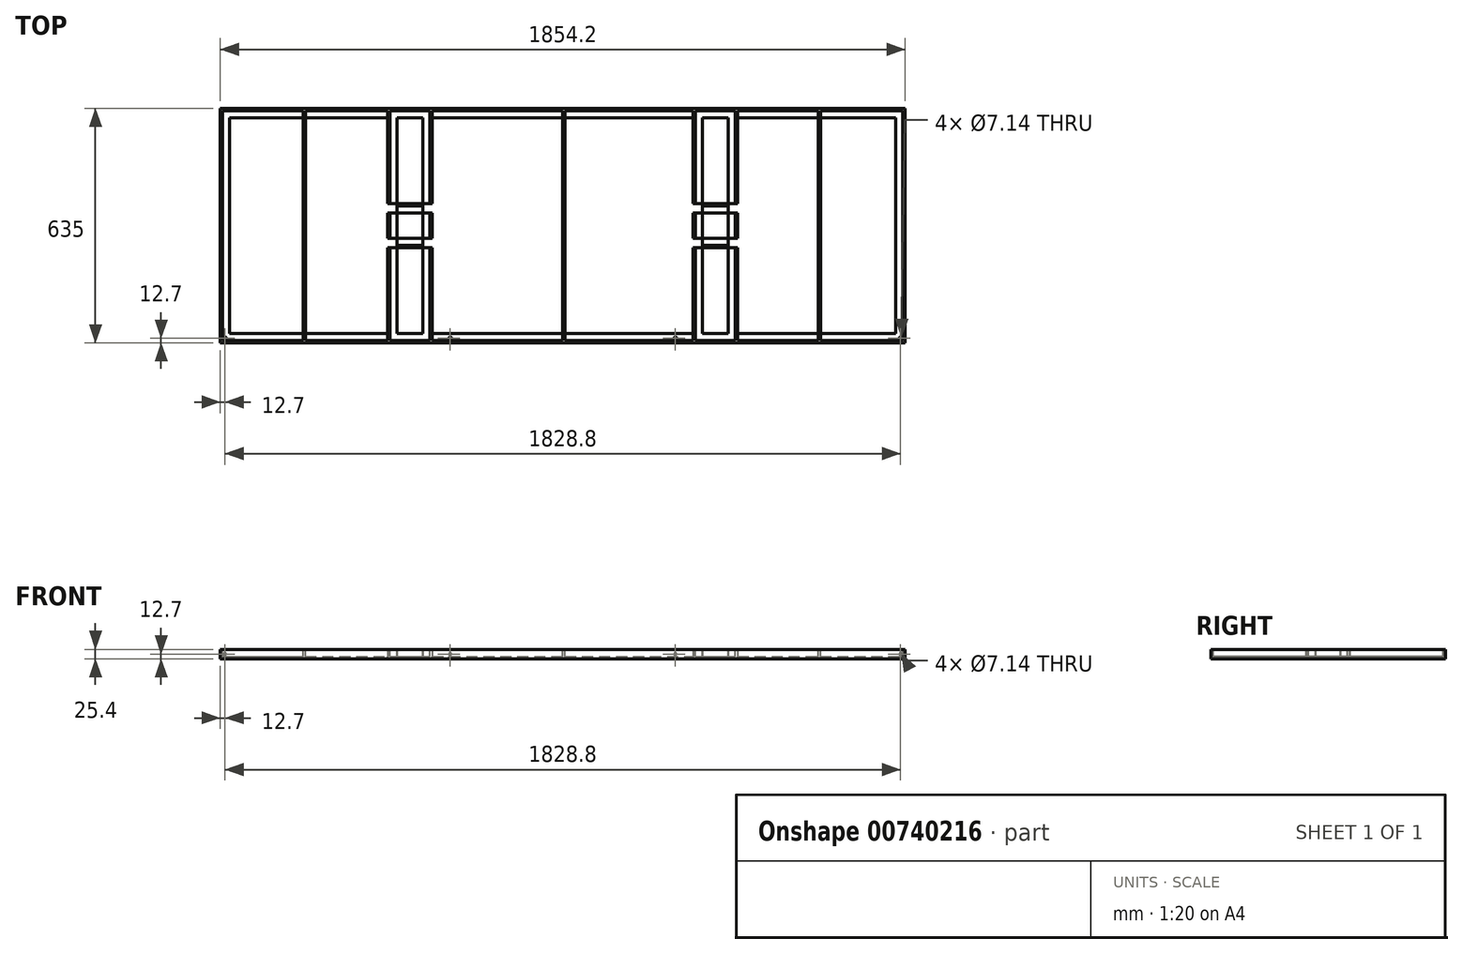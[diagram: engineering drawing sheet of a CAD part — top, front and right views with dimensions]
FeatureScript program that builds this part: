
annotation { "Feature Type Name" : "Feature", "Feature Type Description" : "" }
export const myFeature = defineFeature(function(context is Context, id is Id, definition is map)
    precondition{}
    {
        {
            var Q0;
            Q0=qCreatedBy(makeId("Top.planeOp"),FACE);
            var sketch = newSketch(context, id + "F0", { "sketchPlane" : qUnion([Q0])});
            skLineSegment(sketch, "E0.bottom", {"start": v(0, 0) * mm, "end": v(1854.2, 0) * mm});
            skLineSegment(sketch, "E0.top", {"start": v(0, -25.4) * mm, "end": v(1854.2, -25.4) * mm});
            skLineSegment(sketch, "E0.left", {"start": v(0, 0) * mm, "end": v(0, -25.4) * mm});
            skLineSegment(sketch, "E0.right", {"start": v(1854.2, 0) * mm, "end": v(1854.2, -25.4) * mm});
            skLineSegment(sketch, "E1.bottom", {"start": v(0, 0) * mm, "end": v(25.4, 0) * mm});
            skLineSegment(sketch, "E1.top", {"start": v(0, -635) * mm, "end": v(25.4, -635) * mm});
            skLineSegment(sketch, "E1.left", {"start": v(0, 0) * mm, "end": v(0, -635) * mm});
            skLineSegment(sketch, "E1.right", {"start": v(25.4, 0) * mm, "end": v(25.4, -635) * mm});
            skLineSegment(sketch, "E2.bottom", {"start": v(0, -635) * mm, "end": v(1854.2, -635) * mm});
            skLineSegment(sketch, "E2.top", {"start": v(0, -609.6) * mm, "end": v(1854.2, -609.6) * mm});
            skLineSegment(sketch, "E2.left", {"start": v(0, -635) * mm, "end": v(0, -609.6) * mm});
            skLineSegment(sketch, "E2.right", {"start": v(1854.2, -635) * mm, "end": v(1854.2, -609.6) * mm});
            skLineSegment(sketch, "E3.bottom", {"start": v(1854.2, 0) * mm, "end": v(1828.8, 0) * mm});
            skLineSegment(sketch, "E3.top", {"start": v(1854.2, -635) * mm, "end": v(1828.8, -635) * mm});
            skLineSegment(sketch, "E3.left", {"start": v(1854.2, 0) * mm, "end": v(1854.2, -635) * mm});
            skLineSegment(sketch, "E3.right", {"start": v(1828.8, 0) * mm, "end": v(1828.8, -635) * mm});
            skSolve(sketch);
        }
        {
            var Q0;
            Q0 = qSketchRegion(id + "F0", true);
            extrude(context, id + "F1", {"entities" : qUnion([Q0]), "depth" : 25.4 * mm, "offsetDistance" : 25.4 * mm});
        }
        {
            var Q0;
            Q0=makeQuery(id+"F1.opExtrude","CAP_FACE",FACE,{"disambiguationData":[OSD([sQuery(id+"F0.wireOp",EDGE,"E0.bottom"),sQuery(id+"F0.wireOp",EDGE,"E0.top"),sQuery(id+"F0.wireOp",EDGE,"E1.bottom"),sQuery(id+"F0.wireOp",EDGE,"E1.left"),sQuery(id+"F0.wireOp",EDGE,"E1.right"),sQuery(id+"F0.wireOp",EDGE,"E2.bottom"),sQuery(id+"F0.wireOp",EDGE,"E2.top"),sQuery(id+"F0.wireOp",EDGE,"E2.left"),sQuery(id+"F0.wireOp",EDGE,"E3.bottom"),sQuery(id+"F0.wireOp",EDGE,"E3.top"),sQuery(id+"F0.wireOp",EDGE,"E3.left"),sQuery(id+"F0.wireOp",EDGE,"E3.right")])],"isStart":false});
            var sketch = newSketch(context, id + "F2", { "sketchPlane" : qUnion([Q0])});
            skLineSegment(sketch, "E4.bottom", {"start": v(6.35, -6.35) * mm, "end": v(1847.85, -6.35) * mm});
            skLineSegment(sketch, "E4.top", {"start": v(6.35, -628.65) * mm, "end": v(1847.85, -628.65) * mm});
            skLineSegment(sketch, "E4.left", {"start": v(6.35, -6.35) * mm, "end": v(6.35, -628.65) * mm});
            skLineSegment(sketch, "E4.right", {"start": v(1847.85, -6.35) * mm, "end": v(1847.85, -628.65) * mm});
            skSolve(sketch);
        }
        {
            var Q0;
            Q0=makeQuery(id+"F2.imprint","IMPRINT",FACE,{"disambiguationData":[TD([[makeQuery(id+"F2.imprint","IMPRINT",EDGE,{"derivedFrom":sQuery(id+"F2.wireOp",EDGE,"E4.bottom")}),-1.0]])]});
            extrude(context, id + "F3", {"entities" : qUnion([Q0]), "operationType" : NewBodyOperationType.REMOVE, "oppositeDirection" : true, "depth" : 19.05 * mm, "offsetDistance" : 25.4 * mm});
        }
        {
            var Q0;
            Q0=makeQuery(id+"F1.opExtrude","CAP_FACE",FACE,{"disambiguationData":[OSD([sQuery(id+"F0.wireOp",EDGE,"E0.bottom"),sQuery(id+"F0.wireOp",EDGE,"E0.top"),sQuery(id+"F0.wireOp",EDGE,"E1.bottom"),sQuery(id+"F0.wireOp",EDGE,"E1.left"),sQuery(id+"F0.wireOp",EDGE,"E1.right"),sQuery(id+"F0.wireOp",EDGE,"E2.bottom"),sQuery(id+"F0.wireOp",EDGE,"E2.top"),sQuery(id+"F0.wireOp",EDGE,"E2.left"),sQuery(id+"F0.wireOp",EDGE,"E3.bottom"),sQuery(id+"F0.wireOp",EDGE,"E3.top"),sQuery(id+"F0.wireOp",EDGE,"E3.left"),sQuery(id+"F0.wireOp",EDGE,"E3.right")])],"isStart":true});
            var sketch = newSketch(context, id + "F4", { "sketchPlane" : qUnion([Q0])});
            skLineSegment(sketch, "E5.bottom", {"start": v(548.83, 635) * mm, "end": v(574.23, 635) * mm});
            skLineSegment(sketch, "E5.top", {"start": v(548.83, 0) * mm, "end": v(574.23, 0) * mm});
            skLineSegment(sketch, "E5.left", {"start": v(548.83, 635) * mm, "end": v(548.83, 0) * mm});
            skLineSegment(sketch, "E5.right", {"start": v(574.23, 635) * mm, "end": v(574.23, 0) * mm});
            skLineSegment(sketch, "E6.bottom", {"start": v(1279.96, 635) * mm, "end": v(1305.36, 635) * mm});
            skLineSegment(sketch, "E6.top", {"start": v(1279.96, 0) * mm, "end": v(1305.36, 0) * mm});
            skLineSegment(sketch, "E6.left", {"start": v(1279.96, 635) * mm, "end": v(1279.96, 0) * mm});
            skLineSegment(sketch, "E6.right", {"start": v(1305.36, 635) * mm, "end": v(1305.36, 0) * mm});
            skLineSegment(sketch, "E7.bottom", {"start": v(479, 635) * mm, "end": v(453.6, 635) * mm});
            skLineSegment(sketch, "E7.top", {"start": v(479, 0) * mm, "end": v(453.6, 0) * mm});
            skLineSegment(sketch, "E7.left", {"start": v(479, 635) * mm, "end": v(479, 0) * mm});
            skLineSegment(sketch, "E7.right", {"start": v(453.6, 635) * mm, "end": v(453.6, 0) * mm});
            skLineSegment(sketch, "E8.bottom", {"start": v(1375.2, 635) * mm, "end": v(1400.6, 635) * mm});
            skLineSegment(sketch, "E8.top", {"start": v(1375.2, 0) * mm, "end": v(1400.6, 0) * mm});
            skLineSegment(sketch, "E8.left", {"start": v(1375.2, 635) * mm, "end": v(1375.2, 0) * mm});
            skLineSegment(sketch, "E8.right", {"start": v(1400.6, 635) * mm, "end": v(1400.6, 0) * mm});
            skLineSegment(sketch, "E9.bottom", {"start": v(453.6, 377.02) * mm, "end": v(574.23, 377.02) * mm});
            skLineSegment(sketch, "E9.top", {"start": v(453.6, 351.62) * mm, "end": v(574.23, 351.62) * mm});
            skLineSegment(sketch, "E9.left", {"start": v(453.6, 377.02) * mm, "end": v(453.6, 351.62) * mm});
            skLineSegment(sketch, "E9.right", {"start": v(574.23, 377.02) * mm, "end": v(574.23, 351.62) * mm});
            skLineSegment(sketch, "E10.bottom", {"start": v(453.6, 283.38) * mm, "end": v(574.23, 283.38) * mm});
            skLineSegment(sketch, "E10.top", {"start": v(453.6, 257.98) * mm, "end": v(574.23, 257.98) * mm});
            skLineSegment(sketch, "E10.left", {"start": v(453.6, 283.38) * mm, "end": v(453.6, 257.98) * mm});
            skLineSegment(sketch, "E10.right", {"start": v(574.23, 283.38) * mm, "end": v(574.23, 257.98) * mm});
            skLineSegment(sketch, "E11.bottom", {"start": v(1279.96, 377.02) * mm, "end": v(1400.6, 377.02) * mm});
            skLineSegment(sketch, "E11.top", {"start": v(1279.96, 351.62) * mm, "end": v(1400.6, 351.62) * mm});
            skLineSegment(sketch, "E11.left", {"start": v(1279.96, 377.02) * mm, "end": v(1279.96, 351.62) * mm});
            skLineSegment(sketch, "E11.right", {"start": v(1400.6, 377.02) * mm, "end": v(1400.6, 351.62) * mm});
            skLineSegment(sketch, "E12.bottom", {"start": v(1279.96, 283.38) * mm, "end": v(1400.6, 283.38) * mm});
            skLineSegment(sketch, "E12.top", {"start": v(1279.96, 257.98) * mm, "end": v(1400.6, 257.98) * mm});
            skLineSegment(sketch, "E12.left", {"start": v(1279.96, 283.38) * mm, "end": v(1279.96, 257.98) * mm});
            skLineSegment(sketch, "E12.right", {"start": v(1400.6, 283.38) * mm, "end": v(1400.6, 257.98) * mm});
            skSolve(sketch);
        }
        {
            var Q0;
            {var subQ0=sQuery(id+"F4.wireOp",EDGE,"E9.bottom");var subQ1=sQuery(id+"F4.wireOp",EDGE,"E7.left");var subQ2=makeQuery(id+"F4.imprint","INTERSECT",VERTEX,{"derivedFrom":[subQ1,subQ0]});Q0=makeQuery(id+"F4.imprint","IMPRINT",FACE,{"disambiguationData":[TD([[makeQuery(id+"F4.imprint","IMPRINT",EDGE,{"disambiguationData":[TD([[subQ2,1.0]])],"derivedFrom":subQ1}),-1.0]])]});}
            var Q1;
            {var subQ0=sQuery(id+"F4.wireOp",EDGE,"E7.bottom");Q1=makeQuery(id+"F4.imprint","IMPRINT",FACE,{"disambiguationData":[TD([[makeQuery(id+"F4.imprint","IMPRINT",EDGE,{"derivedFrom":subQ0}),-1.0]])]});}
            var Q2;
            {var subQ0=sQuery(id+"F4.wireOp",EDGE,"E5.bottom");Q2=makeQuery(id+"F4.imprint","IMPRINT",FACE,{"disambiguationData":[TD([[makeQuery(id+"F4.imprint","IMPRINT",EDGE,{"derivedFrom":subQ0}),-1.0]])]});}
            var Q3;
            {var subQ0=sQuery(id+"F4.wireOp",EDGE,"E9.bottom");var subQ1=sQuery(id+"F4.wireOp",EDGE,"E5.left");var subQ2=makeQuery(id+"F4.imprint","INTERSECT",VERTEX,{"derivedFrom":[subQ1,subQ0]});Q3=makeQuery(id+"F4.imprint","IMPRINT",FACE,{"disambiguationData":[TD([[makeQuery(id+"F4.imprint","IMPRINT",EDGE,{"disambiguationData":[TD([[subQ2,1.0]])],"derivedFrom":subQ1}),1.0]])]});}
            var Q4;
            {var subQ5=sQuery(id+"F4.wireOp",EDGE,"E9.right");Q4=makeQuery(id+"F4.imprint","IMPRINT",FACE,{"disambiguationData":[TD([[makeQuery(id+"F4.imprint","IMPRINT",EDGE,{"derivedFrom":subQ5}),-1.0]])]});}
            var Q5;
            {var subQ0=sQuery(id+"F4.wireOp",EDGE,"E9.bottom");var subQ1=sQuery(id+"F4.wireOp",EDGE,"E5.left");var subQ2=makeQuery(id+"F4.imprint","INTERSECT",VERTEX,{"derivedFrom":[subQ1,subQ0]});Q5=makeQuery(id+"F4.imprint","IMPRINT",FACE,{"disambiguationData":[TD([[makeQuery(id+"F4.imprint","IMPRINT",EDGE,{"disambiguationData":[TD([[subQ2,-1.0]])],"derivedFrom":subQ1}),-1.0]])]});}
            var Q6;
            {var subQ5=sQuery(id+"F4.wireOp",EDGE,"E9.left");Q6=makeQuery(id+"F4.imprint","IMPRINT",FACE,{"disambiguationData":[TD([[makeQuery(id+"F4.imprint","IMPRINT",EDGE,{"derivedFrom":subQ5}),1.0]])]});}
            var Q7;
            {var subQ0=sQuery(id+"F4.wireOp",EDGE,"E9.top");var subQ1=sQuery(id+"F4.wireOp",EDGE,"E7.left");var subQ2=makeQuery(id+"F4.imprint","INTERSECT",VERTEX,{"derivedFrom":[subQ1,subQ0]});Q7=makeQuery(id+"F4.imprint","IMPRINT",FACE,{"disambiguationData":[TD([[makeQuery(id+"F4.imprint","IMPRINT",EDGE,{"disambiguationData":[TD([[subQ2,-1.0]])],"derivedFrom":subQ1}),-1.0]])]});}
            var Q8;
            {var subQ0=sQuery(id+"F4.wireOp",EDGE,"E9.top");var subQ1=sQuery(id+"F4.wireOp",EDGE,"E5.left");var subQ2=makeQuery(id+"F4.imprint","INTERSECT",VERTEX,{"derivedFrom":[subQ1,subQ0]});Q8=makeQuery(id+"F4.imprint","IMPRINT",FACE,{"disambiguationData":[TD([[makeQuery(id+"F4.imprint","IMPRINT",EDGE,{"disambiguationData":[TD([[subQ2,-1.0]])],"derivedFrom":subQ1}),1.0]])]});}
            var Q9;
            {var subQ5=sQuery(id+"F4.wireOp",EDGE,"E10.right");Q9=makeQuery(id+"F4.imprint","IMPRINT",FACE,{"disambiguationData":[TD([[makeQuery(id+"F4.imprint","IMPRINT",EDGE,{"derivedFrom":subQ5}),-1.0]])]});}
            var Q10;
            {var subQ0=sQuery(id+"F4.wireOp",EDGE,"E10.bottom");var subQ1=sQuery(id+"F4.wireOp",EDGE,"E5.left");var subQ2=makeQuery(id+"F4.imprint","INTERSECT",VERTEX,{"derivedFrom":[subQ1,subQ0]});Q10=makeQuery(id+"F4.imprint","IMPRINT",FACE,{"disambiguationData":[TD([[makeQuery(id+"F4.imprint","IMPRINT",EDGE,{"disambiguationData":[TD([[subQ2,-1.0]])],"derivedFrom":subQ1}),-1.0]])]});}
            var Q11;
            {var subQ5=sQuery(id+"F4.wireOp",EDGE,"E10.left");Q11=makeQuery(id+"F4.imprint","IMPRINT",FACE,{"disambiguationData":[TD([[makeQuery(id+"F4.imprint","IMPRINT",EDGE,{"derivedFrom":subQ5}),1.0]])]});}
            var Q12;
            {var subQ0=sQuery(id+"F4.wireOp",EDGE,"E10.top");var subQ1=sQuery(id+"F4.wireOp",EDGE,"E7.left");var subQ2=makeQuery(id+"F4.imprint","INTERSECT",VERTEX,{"derivedFrom":[subQ1,subQ0]});Q12=makeQuery(id+"F4.imprint","IMPRINT",FACE,{"disambiguationData":[TD([[makeQuery(id+"F4.imprint","IMPRINT",EDGE,{"disambiguationData":[TD([[subQ2,-1.0]])],"derivedFrom":subQ1}),-1.0]])]});}
            var Q13;
            {var subQ0=sQuery(id+"F4.wireOp",EDGE,"E7.top");Q13=makeQuery(id+"F4.imprint","IMPRINT",FACE,{"disambiguationData":[TD([[makeQuery(id+"F4.imprint","IMPRINT",EDGE,{"derivedFrom":subQ0}),1.0]])]});}
            var Q14;
            {var subQ0=sQuery(id+"F4.wireOp",EDGE,"E5.top");Q14=makeQuery(id+"F4.imprint","IMPRINT",FACE,{"disambiguationData":[TD([[makeQuery(id+"F4.imprint","IMPRINT",EDGE,{"derivedFrom":subQ0}),1.0]])]});}
            var Q15;
            {var subQ0=sQuery(id+"F4.wireOp",EDGE,"E10.top");var subQ1=sQuery(id+"F4.wireOp",EDGE,"E5.left");var subQ2=makeQuery(id+"F4.imprint","INTERSECT",VERTEX,{"derivedFrom":[subQ1,subQ0]});Q15=makeQuery(id+"F4.imprint","IMPRINT",FACE,{"disambiguationData":[TD([[makeQuery(id+"F4.imprint","IMPRINT",EDGE,{"disambiguationData":[TD([[subQ2,-1.0]])],"derivedFrom":subQ1}),1.0]])]});}
            var Q16;
            {var subQ0=sQuery(id+"F4.wireOp",EDGE,"E11.top");var subQ5=sQuery(id+"F4.wireOp",EDGE,"E6.right");var subQ6=makeQuery(id+"F4.imprint","INTERSECT",VERTEX,{"derivedFrom":[subQ5,subQ0]});Q16=makeQuery(id+"F4.imprint","IMPRINT",FACE,{"disambiguationData":[TD([[makeQuery(id+"F4.imprint","IMPRINT",EDGE,{"disambiguationData":[TD([[subQ6,-1.0]])],"derivedFrom":subQ5}),-1.0]])]});}
            var Q17;
            {var subQ0=sQuery(id+"F4.wireOp",EDGE,"E6.bottom");Q17=makeQuery(id+"F4.imprint","IMPRINT",FACE,{"disambiguationData":[TD([[makeQuery(id+"F4.imprint","IMPRINT",EDGE,{"derivedFrom":subQ0}),-1.0]])]});}
            var Q18;
            {var subQ0=sQuery(id+"F4.wireOp",EDGE,"E8.bottom");Q18=makeQuery(id+"F4.imprint","IMPRINT",FACE,{"disambiguationData":[TD([[makeQuery(id+"F4.imprint","IMPRINT",EDGE,{"derivedFrom":subQ0}),-1.0]])]});}
            var Q19;
            {var subQ0=sQuery(id+"F4.wireOp",EDGE,"E11.bottom");var subQ5=sQuery(id+"F4.wireOp",EDGE,"E6.right");var subQ6=makeQuery(id+"F4.imprint","INTERSECT",VERTEX,{"derivedFrom":[subQ5,subQ0]});Q19=makeQuery(id+"F4.imprint","IMPRINT",FACE,{"disambiguationData":[TD([[makeQuery(id+"F4.imprint","IMPRINT",EDGE,{"disambiguationData":[TD([[subQ6,1.0]])],"derivedFrom":subQ5}),-1.0]])]});}
            var Q20;
            {var subQ0=sQuery(id+"F4.wireOp",EDGE,"E11.bottom");var subQ1=sQuery(id+"F4.wireOp",EDGE,"E8.left");var subQ2=makeQuery(id+"F4.imprint","INTERSECT",VERTEX,{"derivedFrom":[subQ1,subQ0]});Q20=makeQuery(id+"F4.imprint","IMPRINT",FACE,{"disambiguationData":[TD([[makeQuery(id+"F4.imprint","IMPRINT",EDGE,{"disambiguationData":[TD([[subQ2,1.0]])],"derivedFrom":subQ1}),1.0]])]});}
            var Q21;
            {var subQ0=sQuery(id+"F4.wireOp",EDGE,"E11.bottom");var subQ1=sQuery(id+"F4.wireOp",EDGE,"E6.right");var subQ2=makeQuery(id+"F4.imprint","INTERSECT",VERTEX,{"derivedFrom":[subQ1,subQ0]});Q21=makeQuery(id+"F4.imprint","IMPRINT",FACE,{"disambiguationData":[TD([[makeQuery(id+"F4.imprint","IMPRINT",EDGE,{"disambiguationData":[TD([[subQ2,-1.0]])],"derivedFrom":subQ1}),1.0]])]});}
            var Q22;
            {var subQ0=sQuery(id+"F4.wireOp",EDGE,"E11.top");var subQ1=sQuery(id+"F4.wireOp",EDGE,"E8.left");var subQ2=makeQuery(id+"F4.imprint","INTERSECT",VERTEX,{"derivedFrom":[subQ1,subQ0]});Q22=makeQuery(id+"F4.imprint","IMPRINT",FACE,{"disambiguationData":[TD([[makeQuery(id+"F4.imprint","IMPRINT",EDGE,{"disambiguationData":[TD([[subQ2,-1.0]])],"derivedFrom":subQ1}),1.0]])]});}
            var Q23;
            {var subQ5=sQuery(id+"F4.wireOp",EDGE,"E11.right");Q23=makeQuery(id+"F4.imprint","IMPRINT",FACE,{"disambiguationData":[TD([[makeQuery(id+"F4.imprint","IMPRINT",EDGE,{"derivedFrom":subQ5}),-1.0]])]});}
            var Q24;
            {var subQ5=sQuery(id+"F4.wireOp",EDGE,"E11.left");Q24=makeQuery(id+"F4.imprint","IMPRINT",FACE,{"disambiguationData":[TD([[makeQuery(id+"F4.imprint","IMPRINT",EDGE,{"derivedFrom":subQ5}),1.0]])]});}
            var Q25;
            {var subQ5=sQuery(id+"F4.wireOp",EDGE,"E12.left");Q25=makeQuery(id+"F4.imprint","IMPRINT",FACE,{"disambiguationData":[TD([[makeQuery(id+"F4.imprint","IMPRINT",EDGE,{"derivedFrom":subQ5}),1.0]])]});}
            var Q26;
            {var subQ0=sQuery(id+"F4.wireOp",EDGE,"E12.bottom");var subQ1=sQuery(id+"F4.wireOp",EDGE,"E6.right");var subQ2=makeQuery(id+"F4.imprint","INTERSECT",VERTEX,{"derivedFrom":[subQ1,subQ0]});Q26=makeQuery(id+"F4.imprint","IMPRINT",FACE,{"disambiguationData":[TD([[makeQuery(id+"F4.imprint","IMPRINT",EDGE,{"disambiguationData":[TD([[subQ2,-1.0]])],"derivedFrom":subQ1}),1.0]])]});}
            var Q27;
            {var subQ5=sQuery(id+"F4.wireOp",EDGE,"E12.right");Q27=makeQuery(id+"F4.imprint","IMPRINT",FACE,{"disambiguationData":[TD([[makeQuery(id+"F4.imprint","IMPRINT",EDGE,{"derivedFrom":subQ5}),-1.0]])]});}
            var Q28;
            {var subQ0=sQuery(id+"F4.wireOp",EDGE,"E12.top");var subQ1=sQuery(id+"F4.wireOp",EDGE,"E8.left");var subQ2=makeQuery(id+"F4.imprint","INTERSECT",VERTEX,{"derivedFrom":[subQ1,subQ0]});Q28=makeQuery(id+"F4.imprint","IMPRINT",FACE,{"disambiguationData":[TD([[makeQuery(id+"F4.imprint","IMPRINT",EDGE,{"disambiguationData":[TD([[subQ2,-1.0]])],"derivedFrom":subQ1}),1.0]])]});}
            var Q29;
            {var subQ0=sQuery(id+"F4.wireOp",EDGE,"E12.top");var subQ5=sQuery(id+"F4.wireOp",EDGE,"E6.right");var subQ7=makeQuery(id+"F4.imprint","INTERSECT",VERTEX,{"derivedFrom":[subQ5,subQ0]});Q29=makeQuery(id+"F4.imprint","IMPRINT",FACE,{"disambiguationData":[TD([[makeQuery(id+"F4.imprint","IMPRINT",EDGE,{"disambiguationData":[TD([[subQ7,-1.0]])],"derivedFrom":subQ5}),-1.0]])]});}
            var Q30;
            {var subQ0=sQuery(id+"F4.wireOp",EDGE,"E6.top");Q30=makeQuery(id+"F4.imprint","IMPRINT",FACE,{"disambiguationData":[TD([[makeQuery(id+"F4.imprint","IMPRINT",EDGE,{"derivedFrom":subQ0}),1.0]])]});}
            var Q31;
            {var subQ0=sQuery(id+"F4.wireOp",EDGE,"E8.top");Q31=makeQuery(id+"F4.imprint","IMPRINT",FACE,{"disambiguationData":[TD([[makeQuery(id+"F4.imprint","IMPRINT",EDGE,{"derivedFrom":subQ0}),1.0]])]});}
            extrude(context, id + "F5", {"entities" : qUnion([Q0, Q1, Q2, Q3, Q4, Q5, Q6, Q7, Q8, Q9, Q10, Q11, Q12, Q13, Q14, Q15, Q16, Q17, Q18, Q19, Q20, Q21, Q22, Q23, Q24, Q25, Q26, Q27, Q28, Q29, Q30, Q31]), "operationType" : NewBodyOperationType.ADD, "oppositeDirection" : true, "depth" : 25.4 * mm, "offsetDistance" : 25.4 * mm});
        }
        {
            var Q0;
            Q0=makeQuery(id+"F5.boolean.opBoolean","MERGE",FACE,{"derivedFrom":[makeQuery(id+"F1.opExtrude","CAP_FACE",FACE,{"disambiguationData":[OSD([sQuery(id+"F0.wireOp",EDGE,"E0.bottom"),sQuery(id+"F0.wireOp",EDGE,"E0.top"),sQuery(id+"F0.wireOp",EDGE,"E1.bottom"),sQuery(id+"F0.wireOp",EDGE,"E1.left"),sQuery(id+"F0.wireOp",EDGE,"E1.right"),sQuery(id+"F0.wireOp",EDGE,"E2.bottom"),sQuery(id+"F0.wireOp",EDGE,"E2.top"),sQuery(id+"F0.wireOp",EDGE,"E2.left"),sQuery(id+"F0.wireOp",EDGE,"E3.bottom"),sQuery(id+"F0.wireOp",EDGE,"E3.top"),sQuery(id+"F0.wireOp",EDGE,"E3.left"),sQuery(id+"F0.wireOp",EDGE,"E3.right")])],"isStart":false}),makeQuery(id+"F5.opExtrude","CAP_FACE",FACE,{"disambiguationData":[OSD([sQuery(id+"F4.wireOp",EDGE,"E5.bottom"),sQuery(id+"F4.wireOp",EDGE,"E5.top"),sQuery(id+"F4.wireOp",EDGE,"E5.left"),sQuery(id+"F4.wireOp",EDGE,"E5.right"),sQuery(id+"F4.wireOp",EDGE,"E7.bottom"),sQuery(id+"F4.wireOp",EDGE,"E7.top"),sQuery(id+"F4.wireOp",EDGE,"E7.left"),sQuery(id+"F4.wireOp",EDGE,"E7.right"),sQuery(id+"F4.wireOp",EDGE,"E9.bottom"),sQuery(id+"F4.wireOp",EDGE,"E9.top"),sQuery(id+"F4.wireOp",EDGE,"E9.left"),sQuery(id+"F4.wireOp",EDGE,"E9.right"),sQuery(id+"F4.wireOp",EDGE,"E10.bottom"),sQuery(id+"F4.wireOp",EDGE,"E10.top"),sQuery(id+"F4.wireOp",EDGE,"E10.left"),sQuery(id+"F4.wireOp",EDGE,"E10.right")])],"isStart":false}),makeQuery(id+"F5.opExtrude","CAP_FACE",FACE,{"disambiguationData":[OSD([sQuery(id+"F4.wireOp",EDGE,"E6.bottom"),sQuery(id+"F4.wireOp",EDGE,"E6.top"),sQuery(id+"F4.wireOp",EDGE,"E6.left"),sQuery(id+"F4.wireOp",EDGE,"E6.right"),sQuery(id+"F4.wireOp",EDGE,"E8.bottom"),sQuery(id+"F4.wireOp",EDGE,"E8.top"),sQuery(id+"F4.wireOp",EDGE,"E8.left"),sQuery(id+"F4.wireOp",EDGE,"E8.right"),sQuery(id+"F4.wireOp",EDGE,"E11.bottom"),sQuery(id+"F4.wireOp",EDGE,"E11.top"),sQuery(id+"F4.wireOp",EDGE,"E11.left"),sQuery(id+"F4.wireOp",EDGE,"E11.right"),sQuery(id+"F4.wireOp",EDGE,"E12.bottom"),sQuery(id+"F4.wireOp",EDGE,"E12.top"),sQuery(id+"F4.wireOp",EDGE,"E12.left"),sQuery(id+"F4.wireOp",EDGE,"E12.right")])],"isStart":false})]});
            var sketch = newSketch(context, id + "F6", { "sketchPlane" : qUnion([Q0])});
            skLineSegment(sketch, "E13.bottom", {"start": v(459.94, -6.35) * mm, "end": v(567.88, -6.35) * mm});
            skLineSegment(sketch, "E13.top", {"start": v(459.94, -257.98) * mm, "end": v(567.88, -257.98) * mm});
            skLineSegment(sketch, "E13.left", {"start": v(459.94, -6.35) * mm, "end": v(459.94, -257.98) * mm});
            skLineSegment(sketch, "E13.right", {"start": v(567.88, -6.35) * mm, "end": v(567.88, -257.98) * mm});
            skLineSegment(sketch, "E14.bottom", {"start": v(459.94, -264.33) * mm, "end": v(567.88, -264.33) * mm});
            skLineSegment(sketch, "E14.top", {"start": v(459.94, -370.67) * mm, "end": v(567.88, -370.67) * mm});
            skLineSegment(sketch, "E14.left", {"start": v(459.94, -264.33) * mm, "end": v(459.94, -370.67) * mm});
            skLineSegment(sketch, "E14.right", {"start": v(567.88, -264.33) * mm, "end": v(567.88, -370.67) * mm});
            skLineSegment(sketch, "E15.bottom", {"start": v(459.94, -377.02) * mm, "end": v(567.88, -377.02) * mm});
            skLineSegment(sketch, "E15.top", {"start": v(459.94, -628.65) * mm, "end": v(567.88, -628.65) * mm});
            skLineSegment(sketch, "E15.left", {"start": v(459.94, -377.02) * mm, "end": v(459.94, -628.65) * mm});
            skLineSegment(sketch, "E15.right", {"start": v(567.88, -377.02) * mm, "end": v(567.88, -628.65) * mm});
            skLineSegment(sketch, "E16.bottom", {"start": v(1286.3, -6.35) * mm, "end": v(1394.24, -6.35) * mm});
            skLineSegment(sketch, "E16.top", {"start": v(1286.3, -257.98) * mm, "end": v(1394.24, -257.98) * mm});
            skLineSegment(sketch, "E16.left", {"start": v(1286.3, -6.35) * mm, "end": v(1286.3, -257.98) * mm});
            skLineSegment(sketch, "E16.right", {"start": v(1394.24, -6.35) * mm, "end": v(1394.24, -257.98) * mm});
            skLineSegment(sketch, "E17.bottom", {"start": v(1286.3, -264.33) * mm, "end": v(1394.24, -264.33) * mm});
            skLineSegment(sketch, "E17.top", {"start": v(1286.3, -370.67) * mm, "end": v(1394.24, -370.67) * mm});
            skLineSegment(sketch, "E17.left", {"start": v(1286.3, -264.33) * mm, "end": v(1286.3, -370.67) * mm});
            skLineSegment(sketch, "E17.right", {"start": v(1394.24, -264.33) * mm, "end": v(1394.24, -370.67) * mm});
            skLineSegment(sketch, "E18.bottom", {"start": v(1286.3, -377.02) * mm, "end": v(1394.24, -377.02) * mm});
            skLineSegment(sketch, "E18.top", {"start": v(1286.3, -628.65) * mm, "end": v(1394.24, -628.65) * mm});
            skLineSegment(sketch, "E18.left", {"start": v(1286.3, -377.02) * mm, "end": v(1286.3, -628.65) * mm});
            skLineSegment(sketch, "E18.right", {"start": v(1394.24, -377.02) * mm, "end": v(1394.24, -628.65) * mm});
            skSolve(sketch);
        }
        {
            var Q0;
            {var subQ4=sQuery(id+"F6.wireOp",EDGE,"E16.left");Q0=makeQuery(id+"F6.imprint","IMPRINT",FACE,{"disambiguationData":[TD([[makeQuery(id+"F6.imprint","IMPRINT",EDGE,{"derivedFrom":subQ4}),1.0]])]});}
            var Q1;
            {var subQ4=sQuery(id+"F6.wireOp",EDGE,"E16.right");Q1=makeQuery(id+"F6.imprint","IMPRINT",FACE,{"disambiguationData":[TD([[makeQuery(id+"F6.imprint","IMPRINT",EDGE,{"derivedFrom":subQ4}),-1.0]])]});}
            var Q2;
            Q2=makeQuery(id+"F6.imprint","IMPRINT",FACE,{"disambiguationData":[TD([[makeQuery(id+"F6.imprint","IMPRINT",EDGE,{"derivedFrom":sQuery(id+"F6.wireOp",EDGE,"E17.bottom")}),-1.0]])]});
            var Q3;
            {var subQ4=sQuery(id+"F6.wireOp",EDGE,"E18.right");Q3=makeQuery(id+"F6.imprint","IMPRINT",FACE,{"disambiguationData":[TD([[makeQuery(id+"F6.imprint","IMPRINT",EDGE,{"derivedFrom":subQ4}),-1.0]])]});}
            var Q4;
            {var subQ4=sQuery(id+"F6.wireOp",EDGE,"E18.left");Q4=makeQuery(id+"F6.imprint","IMPRINT",FACE,{"disambiguationData":[TD([[makeQuery(id+"F6.imprint","IMPRINT",EDGE,{"derivedFrom":subQ4}),1.0]])]});}
            var Q5;
            {var subQ4=sQuery(id+"F6.wireOp",EDGE,"E15.right");Q5=makeQuery(id+"F6.imprint","IMPRINT",FACE,{"disambiguationData":[TD([[makeQuery(id+"F6.imprint","IMPRINT",EDGE,{"derivedFrom":subQ4}),-1.0]])]});}
            var Q6;
            {var subQ4=sQuery(id+"F6.wireOp",EDGE,"E15.left");Q6=makeQuery(id+"F6.imprint","IMPRINT",FACE,{"disambiguationData":[TD([[makeQuery(id+"F6.imprint","IMPRINT",EDGE,{"derivedFrom":subQ4}),1.0]])]});}
            var Q7;
            Q7=makeQuery(id+"F6.imprint","IMPRINT",FACE,{"disambiguationData":[TD([[makeQuery(id+"F6.imprint","IMPRINT",EDGE,{"derivedFrom":sQuery(id+"F6.wireOp",EDGE,"E14.bottom")}),-1.0]])]});
            var Q8;
            {var subQ4=sQuery(id+"F6.wireOp",EDGE,"E13.left");Q8=makeQuery(id+"F6.imprint","IMPRINT",FACE,{"disambiguationData":[TD([[makeQuery(id+"F6.imprint","IMPRINT",EDGE,{"derivedFrom":subQ4}),1.0]])]});}
            var Q9;
            {var subQ4=sQuery(id+"F6.wireOp",EDGE,"E13.right");Q9=makeQuery(id+"F6.imprint","IMPRINT",FACE,{"disambiguationData":[TD([[makeQuery(id+"F6.imprint","IMPRINT",EDGE,{"derivedFrom":subQ4}),-1.0]])]});}
            extrude(context, id + "F7", {"entities" : qUnion([Q0, Q1, Q2, Q3, Q4, Q5, Q6, Q7, Q8, Q9]), "operationType" : NewBodyOperationType.REMOVE, "oppositeDirection" : true, "depth" : 19.05 * mm, "offsetDistance" : 25.4 * mm});
        }
        {
            var Q0;
            Q0=makeQuery(id+"Fk648HPrqjdpP8f_2.boolean.opBoolean","MERGE",FACE,{"derivedFrom":[makeQuery(id+"F5.boolean.opBoolean","MERGE",FACE,{"derivedFrom":[makeQuery(id+"F1.opExtrude","CAP_FACE",FACE,{"disambiguationData":[OSD([sQuery(id+"F0.wireOp",EDGE,"E0.bottom"),sQuery(id+"F0.wireOp",EDGE,"E0.top"),sQuery(id+"F0.wireOp",EDGE,"E1.bottom"),sQuery(id+"F0.wireOp",EDGE,"E1.left"),sQuery(id+"F0.wireOp",EDGE,"E1.right"),sQuery(id+"F0.wireOp",EDGE,"E2.bottom"),sQuery(id+"F0.wireOp",EDGE,"E2.top"),sQuery(id+"F0.wireOp",EDGE,"E2.left"),sQuery(id+"F0.wireOp",EDGE,"E3.bottom"),sQuery(id+"F0.wireOp",EDGE,"E3.top"),sQuery(id+"F0.wireOp",EDGE,"E3.left"),sQuery(id+"F0.wireOp",EDGE,"E3.right")])],"isStart":true}),makeQuery(id+"F5.opExtrude","CAP_FACE",FACE,{"disambiguationData":[OSD([sQuery(id+"F4.wireOp",EDGE,"E5.bottom"),sQuery(id+"F4.wireOp",EDGE,"E5.top"),sQuery(id+"F4.wireOp",EDGE,"E5.left"),sQuery(id+"F4.wireOp",EDGE,"E5.right"),sQuery(id+"F4.wireOp",EDGE,"E7.bottom"),sQuery(id+"F4.wireOp",EDGE,"E7.top"),sQuery(id+"F4.wireOp",EDGE,"E7.left"),sQuery(id+"F4.wireOp",EDGE,"E7.right"),sQuery(id+"F4.wireOp",EDGE,"E9.bottom"),sQuery(id+"F4.wireOp",EDGE,"E9.top"),sQuery(id+"F4.wireOp",EDGE,"E9.left"),sQuery(id+"F4.wireOp",EDGE,"E9.right"),sQuery(id+"F4.wireOp",EDGE,"E10.bottom"),sQuery(id+"F4.wireOp",EDGE,"E10.top"),sQuery(id+"F4.wireOp",EDGE,"E10.left"),sQuery(id+"F4.wireOp",EDGE,"E10.right")])],"isStart":true}),makeQuery(id+"F5.opExtrude","CAP_FACE",FACE,{"disambiguationData":[OSD([sQuery(id+"F4.wireOp",EDGE,"E6.bottom"),sQuery(id+"F4.wireOp",EDGE,"E6.top"),sQuery(id+"F4.wireOp",EDGE,"E6.left"),sQuery(id+"F4.wireOp",EDGE,"E6.right"),sQuery(id+"F4.wireOp",EDGE,"E8.bottom"),sQuery(id+"F4.wireOp",EDGE,"E8.top"),sQuery(id+"F4.wireOp",EDGE,"E8.left"),sQuery(id+"F4.wireOp",EDGE,"E8.right"),sQuery(id+"F4.wireOp",EDGE,"E11.bottom"),sQuery(id+"F4.wireOp",EDGE,"E11.top"),sQuery(id+"F4.wireOp",EDGE,"E11.left"),sQuery(id+"F4.wireOp",EDGE,"E11.right"),sQuery(id+"F4.wireOp",EDGE,"E12.bottom"),sQuery(id+"F4.wireOp",EDGE,"E12.top"),sQuery(id+"F4.wireOp",EDGE,"E12.left"),sQuery(id+"F4.wireOp",EDGE,"E12.right")])],"isStart":true})]}),makeQuery(id+"Fk648HPrqjdpP8f_2.opExtrude","CAP_FACE",FACE,{"disambiguationData":[OSD([sQuery(id+"FQ27V673fwc3ves_2.wireOp",EDGE,"73UN0u5f-LYI8-i5Pt-mgwE-1p8WNd5GUxVN.bottom"),sQuery(id+"FQ27V673fwc3ves_2.wireOp",EDGE,"73UN0u5f-LYI8-i5Pt-mgwE-1p8WNd5GUxVN.top"),sQuery(id+"FQ27V673fwc3ves_2.wireOp",EDGE,"73UN0u5f-LYI8-i5Pt-mgwE-1p8WNd5GUxVN.left"),sQuery(id+"FQ27V673fwc3ves_2.wireOp",EDGE,"73UN0u5f-LYI8-i5Pt-mgwE-1p8WNd5GUxVN.right")])],"isStart":true}),makeQuery(id+"Fk648HPrqjdpP8f_2.opExtrude","CAP_FACE",FACE,{"disambiguationData":[OSD([sQuery(id+"FQ27V673fwc3ves_2.wireOp",EDGE,"lJe73GXE-Nq5f-4z6N-qGH3-wGdDw6EI5nSz.bottom"),sQuery(id+"FQ27V673fwc3ves_2.wireOp",EDGE,"lJe73GXE-Nq5f-4z6N-qGH3-wGdDw6EI5nSz.top"),sQuery(id+"FQ27V673fwc3ves_2.wireOp",EDGE,"lJe73GXE-Nq5f-4z6N-qGH3-wGdDw6EI5nSz.left"),sQuery(id+"FQ27V673fwc3ves_2.wireOp",EDGE,"lJe73GXE-Nq5f-4z6N-qGH3-wGdDw6EI5nSz.right")])],"isStart":true})]});
            var sketch = newSketch(context, id + "F8", { "sketchPlane" : qUnion([Q0])});
            skCircle(sketch, "E19", {"center": v(12.7, 622.3) * mm, "radius": 3.57 * mm});
            skCircle(sketch, "E20.1.0.0", {"center": v(622.3, 622.3) * mm, "radius": 3.57 * mm});
            skCircle(sketch, "E20.2.0.0", {"center": v(1231.9, 622.3) * mm, "radius": 3.57 * mm});
            skCircle(sketch, "E20.3.0.0", {"center": v(1841.5, 622.3) * mm, "radius": 3.57 * mm});
            skLineSegment(sketch, "E20.direction1", {"start": v(12.7, 622.3) * mm, "end": v(622.3, 622.3) * mm, "construction": true});
            skLineSegment(sketch, "E20.direction2", {"start": v(12.7, 622.3) * mm, "end": v(12.7, 12.7) * mm, "construction": true});
            skSolve(sketch);
        }
        {
            var Q0;
            Q0=makeQuery(id+"F8.imprint","IMPRINT",FACE,{"disambiguationData":[TD([[makeQuery(id+"F8.imprint","IMPRINT",EDGE,{"derivedFrom":sQuery(id+"F8.wireOp",EDGE,"E19")}),1.0]])]});
            var Q1;
            Q1=makeQuery(id+"F8.imprint","IMPRINT",FACE,{"disambiguationData":[TD([[makeQuery(id+"F8.imprint","IMPRINT",EDGE,{"derivedFrom":sQuery(id+"F8.wireOp",EDGE,"E20.1.0.0")}),1.0]])]});
            var Q2;
            Q2=makeQuery(id+"F8.imprint","IMPRINT",FACE,{"disambiguationData":[TD([[makeQuery(id+"F8.imprint","IMPRINT",EDGE,{"derivedFrom":sQuery(id+"F8.wireOp",EDGE,"E20.2.0.0")}),1.0]])]});
            var Q3;
            Q3=makeQuery(id+"F8.imprint","IMPRINT",FACE,{"disambiguationData":[TD([[makeQuery(id+"F8.imprint","IMPRINT",EDGE,{"derivedFrom":sQuery(id+"F8.wireOp",EDGE,"E20.3.0.0")}),1.0]])]});
            var Q4;
            Q4=makeQuery(id+"F8.imprint","IMPRINT",FACE,{"disambiguationData":[TD([[makeQuery(id+"F8.imprint","IMPRINT",EDGE,{"derivedFrom":sQuery(id+"F8.wireOp",EDGE,"E20.4.0.0")}),1.0]])]});
            var Q5;
            Q5=makeQuery(id+"F8.imprint","IMPRINT",FACE,{"disambiguationData":[TD([[makeQuery(id+"F8.imprint","IMPRINT",EDGE,{"derivedFrom":sQuery(id+"F8.wireOp",EDGE,"E20.4.1.0")}),1.0]])]});
            var Q6;
            Q6=makeQuery(id+"F8.imprint","IMPRINT",FACE,{"disambiguationData":[TD([[makeQuery(id+"F8.imprint","IMPRINT",EDGE,{"derivedFrom":sQuery(id+"F8.wireOp",EDGE,"E20.3.1.0")}),1.0]])]});
            var Q7;
            Q7=makeQuery(id+"F8.imprint","IMPRINT",FACE,{"disambiguationData":[TD([[makeQuery(id+"F8.imprint","IMPRINT",EDGE,{"derivedFrom":sQuery(id+"F8.wireOp",EDGE,"E20.2.1.0")}),1.0]])]});
            var Q8;
            Q8=makeQuery(id+"F8.imprint","IMPRINT",FACE,{"disambiguationData":[TD([[makeQuery(id+"F8.imprint","IMPRINT",EDGE,{"derivedFrom":sQuery(id+"F8.wireOp",EDGE,"E20.1.1.0")}),1.0]])]});
            var Q9;
            Q9=makeQuery(id+"F8.imprint","IMPRINT",FACE,{"disambiguationData":[TD([[makeQuery(id+"F8.imprint","IMPRINT",EDGE,{"derivedFrom":sQuery(id+"F8.wireOp",EDGE,"E20.0.1.0")}),1.0]])]});
            extrude(context, id + "F9", {"entities" : qUnion([Q0, Q1, Q2, Q3, Q4, Q5, Q6, Q7, Q8, Q9]), "operationType" : NewBodyOperationType.REMOVE, "oppositeDirection" : true, "depth" : 25.4 * mm, "offsetDistance" : 25.4 * mm});
        }
        {
            var Q0;
            Q0=makeQuery(id+"F1.opExtrude","SWEPT_FACE",FACE,{"disambiguationData":[OSD([sQuery(id+"F0.wireOp",EDGE,"E0.bottom"),sQuery(id+"F0.wireOp",EDGE,"E1.bottom"),sQuery(id+"F0.wireOp",EDGE,"E3.bottom")])]});
            var sketch = newSketch(context, id + "F10", { "sketchPlane" : qUnion([Q0])});
            skCircle(sketch, "E21", {"center": v(-1841.5, 12.7) * mm, "radius": 3.57 * mm});
            skCircle(sketch, "E22.1.0.0", {"center": v(-1231.9, 12.7) * mm, "radius": 3.57 * mm});
            skCircle(sketch, "E22.2.0.0", {"center": v(-622.3, 12.7) * mm, "radius": 3.57 * mm});
            skCircle(sketch, "E22.3.0.0", {"center": v(-12.7, 12.7) * mm, "radius": 3.57 * mm});
            skLineSegment(sketch, "E22.direction1", {"start": v(-1841.5, 12.7) * mm, "end": v(-1231.9, 12.7) * mm, "construction": true});
            skSolve(sketch);
        }
        {
            var Q0;
            Q0=makeQuery(id+"F10.imprint","IMPRINT",FACE,{"disambiguationData":[TD([[makeQuery(id+"F10.imprint","IMPRINT",EDGE,{"derivedFrom":sQuery(id+"F10.wireOp",EDGE,"E21")}),1.0]])]});
            var Q1;
            Q1=makeQuery(id+"F10.imprint","IMPRINT",FACE,{"disambiguationData":[TD([[makeQuery(id+"F10.imprint","IMPRINT",EDGE,{"derivedFrom":sQuery(id+"F10.wireOp",EDGE,"E22.1.0.0")}),1.0]])]});
            var Q2;
            Q2=makeQuery(id+"F10.imprint","IMPRINT",FACE,{"disambiguationData":[TD([[makeQuery(id+"F10.imprint","IMPRINT",EDGE,{"derivedFrom":sQuery(id+"F10.wireOp",EDGE,"E22.2.0.0")}),1.0]])]});
            var Q3;
            Q3=makeQuery(id+"F10.imprint","IMPRINT",FACE,{"disambiguationData":[TD([[makeQuery(id+"F10.imprint","IMPRINT",EDGE,{"derivedFrom":sQuery(id+"F10.wireOp",EDGE,"E22.3.0.0")}),1.0]])]});
            extrude(context, id + "F11", {"entities" : qUnion([Q0, Q1, Q2, Q3]), "operationType" : NewBodyOperationType.REMOVE, "oppositeDirection" : true, "depth" : 25.4 * mm, "offsetDistance" : 25.4 * mm});
        }
        {
            var Q0;
            Q0=makeQuery(id+"F5.boolean.opBoolean","MERGE",FACE,{"derivedFrom":[makeQuery(id+"F1.opExtrude","CAP_FACE",FACE,{"disambiguationData":[OSD([sQuery(id+"F0.wireOp",EDGE,"E0.bottom"),sQuery(id+"F0.wireOp",EDGE,"E0.top"),sQuery(id+"F0.wireOp",EDGE,"E1.bottom"),sQuery(id+"F0.wireOp",EDGE,"E1.left"),sQuery(id+"F0.wireOp",EDGE,"E1.right"),sQuery(id+"F0.wireOp",EDGE,"E2.bottom"),sQuery(id+"F0.wireOp",EDGE,"E2.top"),sQuery(id+"F0.wireOp",EDGE,"E2.left"),sQuery(id+"F0.wireOp",EDGE,"E3.bottom"),sQuery(id+"F0.wireOp",EDGE,"E3.top"),sQuery(id+"F0.wireOp",EDGE,"E3.left"),sQuery(id+"F0.wireOp",EDGE,"E3.right")])],"isStart":false}),makeQuery(id+"F5.opExtrude","CAP_FACE",FACE,{"disambiguationData":[OSD([sQuery(id+"F4.wireOp",EDGE,"E5.bottom"),sQuery(id+"F4.wireOp",EDGE,"E5.top"),sQuery(id+"F4.wireOp",EDGE,"E5.left"),sQuery(id+"F4.wireOp",EDGE,"E5.right"),sQuery(id+"F4.wireOp",EDGE,"E7.bottom"),sQuery(id+"F4.wireOp",EDGE,"E7.top"),sQuery(id+"F4.wireOp",EDGE,"E7.left"),sQuery(id+"F4.wireOp",EDGE,"E7.right"),sQuery(id+"F4.wireOp",EDGE,"E9.bottom"),sQuery(id+"F4.wireOp",EDGE,"E9.top"),sQuery(id+"F4.wireOp",EDGE,"E9.left"),sQuery(id+"F4.wireOp",EDGE,"E9.right"),sQuery(id+"F4.wireOp",EDGE,"E10.bottom"),sQuery(id+"F4.wireOp",EDGE,"E10.top"),sQuery(id+"F4.wireOp",EDGE,"E10.left"),sQuery(id+"F4.wireOp",EDGE,"E10.right")])],"isStart":false}),makeQuery(id+"F5.opExtrude","CAP_FACE",FACE,{"disambiguationData":[OSD([sQuery(id+"F4.wireOp",EDGE,"E6.bottom"),sQuery(id+"F4.wireOp",EDGE,"E6.top"),sQuery(id+"F4.wireOp",EDGE,"E6.left"),sQuery(id+"F4.wireOp",EDGE,"E6.right"),sQuery(id+"F4.wireOp",EDGE,"E8.bottom"),sQuery(id+"F4.wireOp",EDGE,"E8.top"),sQuery(id+"F4.wireOp",EDGE,"E8.left"),sQuery(id+"F4.wireOp",EDGE,"E8.right"),sQuery(id+"F4.wireOp",EDGE,"E11.bottom"),sQuery(id+"F4.wireOp",EDGE,"E11.top"),sQuery(id+"F4.wireOp",EDGE,"E11.left"),sQuery(id+"F4.wireOp",EDGE,"E11.right"),sQuery(id+"F4.wireOp",EDGE,"E12.bottom"),sQuery(id+"F4.wireOp",EDGE,"E12.top"),sQuery(id+"F4.wireOp",EDGE,"E12.left"),sQuery(id+"F4.wireOp",EDGE,"E12.right")])],"isStart":false})]});
            var sketch = newSketch(context, id + "F12", { "sketchPlane" : qUnion([Q0])});
            skLineSegment(sketch, "E23.bottom", {"start": v(229.6, -6.35) * mm, "end": v(230.35, -6.35) * mm});
            skLineSegment(sketch, "E23.top", {"start": v(229.6, -628.65) * mm, "end": v(230.35, -628.65) * mm});
            skLineSegment(sketch, "E23.left", {"start": v(230.35, -6.35) * mm, "end": v(230.35, -628.65) * mm});
            skLineSegment(sketch, "E24.bottom", {"start": v(1618.27, -6.35) * mm, "end": v(1624.62, -6.35) * mm});
            skLineSegment(sketch, "E24.top", {"start": v(1618.27, -628.65) * mm, "end": v(1624.62, -628.65) * mm});
            skLineSegment(sketch, "E24.right", {"start": v(1624.62, -6.35) * mm, "end": v(1624.62, -628.65) * mm});
            skLineSegment(sketch, "E25.bottom", {"start": v(927.1, -6.35) * mm, "end": v(933.44, -6.35) * mm});
            skLineSegment(sketch, "E25.top", {"start": v(927.1, -628.65) * mm, "end": v(933.44, -628.65) * mm});
            skLineSegment(sketch, "E25.left", {"start": v(927.1, -6.35) * mm, "end": v(927.1, -628.65) * mm});
            skLineSegment(sketch, "E25.right", {"start": v(933.44, -6.35) * mm, "end": v(933.44, -628.65) * mm});
            skLineSegment(sketch, "E26.bottom", {"start": v(224, -6.35) * mm, "end": v(230.35, -6.35) * mm});
            skLineSegment(sketch, "E26.top", {"start": v(224, -628.65) * mm, "end": v(230.35, -628.65) * mm});
            skLineSegment(sketch, "E26.left", {"start": v(224, -6.35) * mm, "end": v(224, -628.65) * mm});
            skLineSegment(sketch, "E27.left", {"start": v(1618.27, -6.35) * mm, "end": v(1618.27, -628.65) * mm});
            skSolve(sketch);
        }
        {
            var Q0;
            {var subQ13=sQuery(id+"F12.wireOp",EDGE,"E26.left");Q0=makeQuery(id+"F12.imprint","IMPRINT",FACE,{"disambiguationData":[TD([[makeQuery(id+"F12.imprint","IMPRINT",EDGE,{"derivedFrom":subQ13}),1.0]])]});}
            var Q1;
            Q1=makeQuery(id+"F12.imprint","IMPRINT",FACE,{"disambiguationData":[TD([[makeQuery(id+"F12.imprint","IMPRINT",EDGE,{"derivedFrom":sQuery(id+"F12.wireOp",EDGE,"E25.bottom")}),-1.0]])]});
            var Q2;
            Q2=makeQuery(id+"F12.imprint","IMPRINT",FACE,{"disambiguationData":[TD([[makeQuery(id+"F12.imprint","IMPRINT",EDGE,{"derivedFrom":sQuery(id+"F12.wireOp",EDGE,"E24.bottom")}),-1.0]])]});
            extrude(context, id + "F13", {"entities" : qUnion([Q0, Q1, Q2]), "operationType" : NewBodyOperationType.ADD, "oppositeDirection" : true, "depth" : 25.4 * mm, "offsetDistance" : 25.4 * mm});
        }
    });
